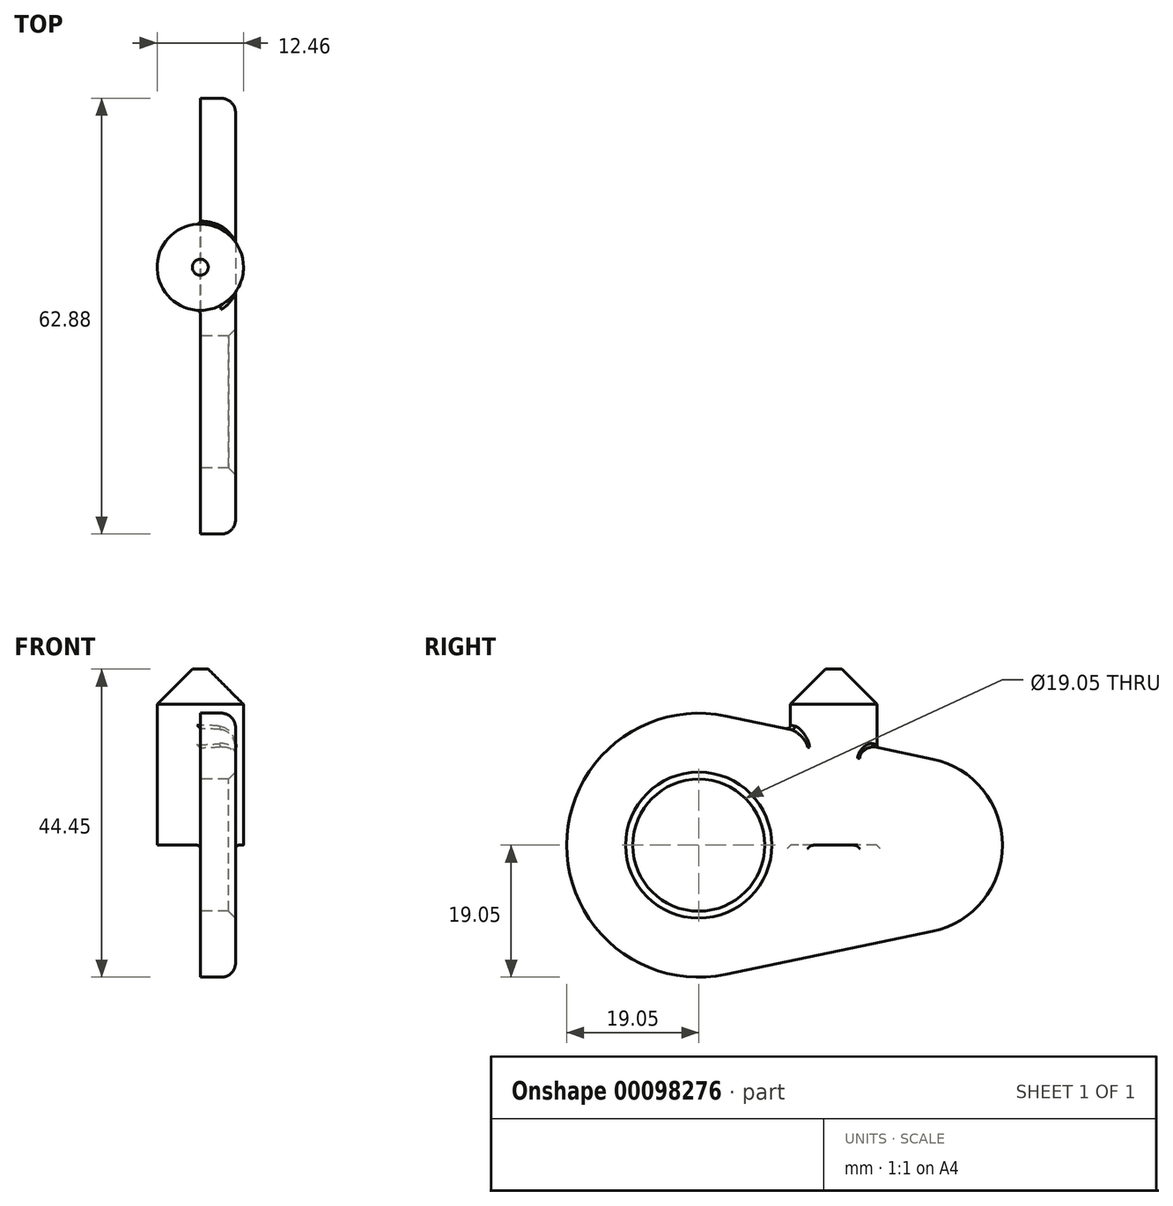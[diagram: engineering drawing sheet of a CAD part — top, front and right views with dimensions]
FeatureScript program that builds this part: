
annotation { "Feature Type Name" : "Feature", "Feature Type Description" : "" }
export const myFeature = defineFeature(function(context is Context, id is Id, definition is map)
    precondition{}
    {
        {
            var Q0;
            Q0=qCreatedBy(makeId("Right.planeOp"),FACE);
            var sketch = newSketch(context, id + "F0", { "sketchPlane" : qUnion([Q0])});
            skArc(sketch, "E0", {"start": v(3.89, 18.65) * mm, "mid": v(-19.05, 0) * mm, "end": v(3.89, -18.65) * mm});
            skLineSegment(sketch, "E1", {"start": v(3.89, 18.65) * mm, "end": v(33.72, 12.43) * mm});
            skLineSegment(sketch, "E2", {"start": v(3.89, -18.65) * mm, "end": v(33.72, -12.43) * mm});
            skCircle(sketch, "E3", {"center": v(0, 0) * mm, "radius": 9.53 * mm});
            skArc(sketch, "E4", {"start": v(33.72, -12.43) * mm, "mid": v(43.83, 0) * mm, "end": v(33.72, 12.43) * mm});
            skSolve(sketch);
        }
        {
            var Q0;
            Q0=makeQuery(id+"F0.imprint","IMPRINT",FACE,{"disambiguationData":[TD([[makeQuery(id+"F0.imprint","IMPRINT",EDGE,{"derivedFrom":sQuery(id+"F0.wireOp",EDGE,"E0")}),1.0]])]});
            extrude(context, id + "F1", {"entities" : qUnion([Q0]), "depth" : 5.08 * mm});
        }
        {
            var Q0;
            Q0=makeQuery(id+"F1.opExtrude","CAP_EDGE",EDGE,{"disambiguationData":[OSD([sQuery(id+"F0.wireOp",EDGE,"E2")])],"isStart":false});
            var Q1;
            Q1=makeQuery(id+"F1.opExtrude","CAP_EDGE",EDGE,{"disambiguationData":[OSD([sQuery(id+"F0.wireOp",EDGE,"E4")])],"isStart":false});
            var Q2;
            Q2=makeQuery(id+"F1.opExtrude","CAP_EDGE",EDGE,{"disambiguationData":[OSD([sQuery(id+"F0.wireOp",EDGE,"E1")])],"isStart":false});
            var Q3;
            Q3=makeQuery(id+"F1.opExtrude","CAP_EDGE",EDGE,{"disambiguationData":[OSD([sQuery(id+"F0.wireOp",EDGE,"E0")])],"isStart":false});
            fillet(context, id + "F2", {"entities" : qUnion([Q0, Q1, Q2, Q3]), "radius" : 2.03 * mm, "tangentPropagation" : true, "allowEdgeOverflow" : false});
        }
        {
            var Q0;
            Q0=makeQuery(id+"F1.opExtrude","CAP_EDGE",EDGE,{"disambiguationData":[OSD([sQuery(id+"F0.wireOp",EDGE,"E3")])],"isStart":false});
            chamfer(context, id + "F3", {"entities" : qUnion([Q0]), "width" : 1.02 * mm, "tangentPropagation" : true});
        }
        {
            var Q0;
            Q0=qCreatedBy(makeId("Top.planeOp"),FACE);
            var sketch = newSketch(context, id + "F4", { "sketchPlane" : qUnion([Q0])});
            skCircle(sketch, "E5", {"center": v(0, 19.47) * mm, "radius": 6.23 * mm});
            skSolve(sketch);
        }
        {
            var Q0;
            Q0=makeQuery(id+"F4.imprint","IMPRINT",FACE,{"disambiguationData":[TD([[makeQuery(id+"F4.imprint","IMPRINT",EDGE,{"derivedFrom":sQuery(id+"F4.wireOp",EDGE,"E5")}),1.0]])]});
            extrude(context, id + "F5", {"entities" : qUnion([Q0]), "operationType" : NewBodyOperationType.ADD, "depth" : 25.4 * mm});
        }
        {
            var Q0;
            Q0=makeQuery(id+"F5.boolean.opBoolean","INTERSECT",EDGE,{"disambiguationData":[OD(0.0)],"derivedFrom":[makeQuery(id+"F1.opExtrude","CAP_FACE",FACE,{"disambiguationData":[OSD([sQuery(id+"F0.wireOp",EDGE,"E0"),sQuery(id+"F0.wireOp",EDGE,"E1"),sQuery(id+"F0.wireOp",EDGE,"E2"),sQuery(id+"F0.wireOp",EDGE,"E3"),sQuery(id+"F0.wireOp",EDGE,"E4")])],"isStart":false}),makeQuery(id+"F5.opExtrude","SWEPT_FACE",FACE,{"disambiguationData":[OSD([sQuery(id+"F4.wireOp",EDGE,"E5")])]})]});
            var Q1;
            Q1=makeQuery(id+"F5.boolean.opBoolean","INTERSECT",EDGE,{"disambiguationData":[OD(0.0)],"derivedFrom":[makeQuery(id+"F2.opFillet","BLEND_FACE",FACE,{"disambiguationData":[OSD([sQuery(id+"F0.wireOp",EDGE,"E1")])]}),makeQuery(id+"F5.opExtrude","SWEPT_FACE",FACE,{"disambiguationData":[OSD([sQuery(id+"F4.wireOp",EDGE,"E5")])]})]});
            var Q2;
            Q2=makeQuery(id+"F5.boolean.opBoolean","INTERSECT",EDGE,{"disambiguationData":[OD(0.0)],"derivedFrom":[makeQuery(id+"F1.opExtrude","SWEPT_FACE",FACE,{"disambiguationData":[OSD([sQuery(id+"F0.wireOp",EDGE,"E1")])]}),makeQuery(id+"F5.opExtrude","SWEPT_FACE",FACE,{"disambiguationData":[OSD([sQuery(id+"F4.wireOp",EDGE,"E5")])]})]});
            var Q3;
            Q3=makeQuery(id+"F5.boolean.opBoolean","INTERSECT",EDGE,{"disambiguationData":[OD(1.0)],"derivedFrom":[makeQuery(id+"F1.opExtrude","CAP_FACE",FACE,{"disambiguationData":[OSD([sQuery(id+"F0.wireOp",EDGE,"E0"),sQuery(id+"F0.wireOp",EDGE,"E1"),sQuery(id+"F0.wireOp",EDGE,"E2"),sQuery(id+"F0.wireOp",EDGE,"E3"),sQuery(id+"F0.wireOp",EDGE,"E4")])],"isStart":false}),makeQuery(id+"F5.opExtrude","SWEPT_FACE",FACE,{"disambiguationData":[OSD([sQuery(id+"F4.wireOp",EDGE,"E5")])]})]});
            var Q4;
            Q4=makeQuery(id+"F5.boolean.opBoolean","INTERSECT",EDGE,{"disambiguationData":[OD(1.0)],"derivedFrom":[makeQuery(id+"F2.opFillet","BLEND_FACE",FACE,{"disambiguationData":[OSD([sQuery(id+"F0.wireOp",EDGE,"E1")])]}),makeQuery(id+"F5.opExtrude","SWEPT_FACE",FACE,{"disambiguationData":[OSD([sQuery(id+"F4.wireOp",EDGE,"E5")])]})]});
            var Q5;
            Q5=makeQuery(id+"F5.boolean.opBoolean","INTERSECT",EDGE,{"disambiguationData":[OD(1.0)],"derivedFrom":[makeQuery(id+"F1.opExtrude","SWEPT_FACE",FACE,{"disambiguationData":[OSD([sQuery(id+"F0.wireOp",EDGE,"E1")])]}),makeQuery(id+"F5.opExtrude","SWEPT_FACE",FACE,{"disambiguationData":[OSD([sQuery(id+"F4.wireOp",EDGE,"E5")])]})]});
            var Q6;
            Q6=makeQuery(id+"F5.boolean.opBoolean","INTERSECT",EDGE,{"disambiguationData":[OD(1.0)],"derivedFrom":[makeQuery(id+"F1.opExtrude","CAP_FACE",FACE,{"disambiguationData":[OSD([sQuery(id+"F0.wireOp",EDGE,"E0"),sQuery(id+"F0.wireOp",EDGE,"E1"),sQuery(id+"F0.wireOp",EDGE,"E2"),sQuery(id+"F0.wireOp",EDGE,"E3"),sQuery(id+"F0.wireOp",EDGE,"E4")])],"isStart":true}),makeQuery(id+"F5.opExtrude","SWEPT_FACE",FACE,{"disambiguationData":[OSD([sQuery(id+"F4.wireOp",EDGE,"E5")])]})]});
            var Q7;
            Q7=makeQuery(id+"F5.boolean.opBoolean","INTERSECT",EDGE,{"disambiguationData":[OD(0.0)],"derivedFrom":[makeQuery(id+"F1.opExtrude","CAP_FACE",FACE,{"disambiguationData":[OSD([sQuery(id+"F0.wireOp",EDGE,"E0"),sQuery(id+"F0.wireOp",EDGE,"E1"),sQuery(id+"F0.wireOp",EDGE,"E2"),sQuery(id+"F0.wireOp",EDGE,"E3"),sQuery(id+"F0.wireOp",EDGE,"E4")])],"isStart":true}),makeQuery(id+"F5.opExtrude","SWEPT_FACE",FACE,{"disambiguationData":[OSD([sQuery(id+"F4.wireOp",EDGE,"E5")])]})]});
            var Q8;
            Q8=makeQuery(id+"F5.boolean.opBoolean","INTERSECT",EDGE,{"derivedFrom":[makeQuery(id+"F1.opExtrude","CAP_FACE",FACE,{"disambiguationData":[OSD([sQuery(id+"F0.wireOp",EDGE,"E0"),sQuery(id+"F0.wireOp",EDGE,"E1"),sQuery(id+"F0.wireOp",EDGE,"E2"),sQuery(id+"F0.wireOp",EDGE,"E3"),sQuery(id+"F0.wireOp",EDGE,"E4")])],"isStart":true}),makeQuery(id+"F5.opExtrude","CAP_FACE",FACE,{"disambiguationData":[OSD([sQuery(id+"F4.wireOp",EDGE,"E5")])],"isStart":true})]});
            var Q9;
            Q9=makeQuery(id+"F5.boolean.opBoolean","INTERSECT",EDGE,{"derivedFrom":[makeQuery(id+"F1.opExtrude","CAP_FACE",FACE,{"disambiguationData":[OSD([sQuery(id+"F0.wireOp",EDGE,"E0"),sQuery(id+"F0.wireOp",EDGE,"E1"),sQuery(id+"F0.wireOp",EDGE,"E2"),sQuery(id+"F0.wireOp",EDGE,"E3"),sQuery(id+"F0.wireOp",EDGE,"E4")])],"isStart":false}),makeQuery(id+"F5.opExtrude","CAP_FACE",FACE,{"disambiguationData":[OSD([sQuery(id+"F4.wireOp",EDGE,"E5")])],"isStart":true})]});
            fillet(context, id + "F6", {"entities" : qUnion([Q0, Q1, Q2, Q3, Q4, Q5, Q6, Q7, Q8, Q9]), "radius" : 0.5 * mm, "tangentPropagation" : true, "allowEdgeOverflow" : false});
        }
        {
            var Q0;
            Q0=makeQuery(id+"F5.opExtrude","CAP_EDGE",EDGE,{"disambiguationData":[OSD([sQuery(id+"F4.wireOp",EDGE,"E5")])],"isStart":false});
            chamfer(context, id + "F7", {"entities" : qUnion([Q0]), "width" : 5.08 * mm, "tangentPropagation" : true});
        }
    });
